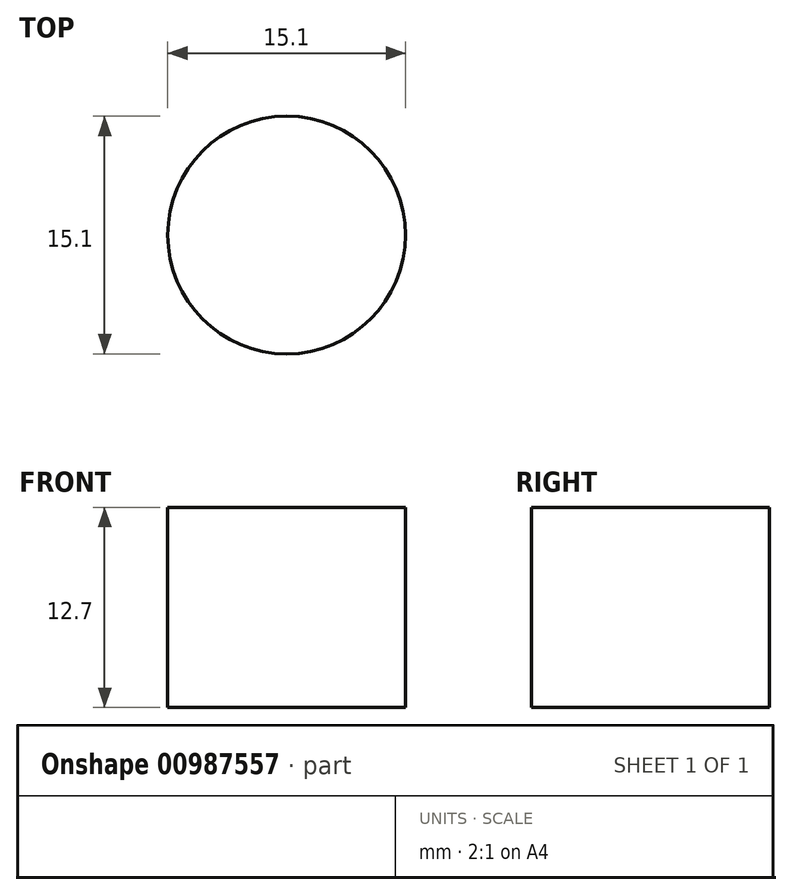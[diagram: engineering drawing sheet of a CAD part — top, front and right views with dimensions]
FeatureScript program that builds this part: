
annotation { "Feature Type Name" : "Feature", "Feature Type Description" : "" }
export const myFeature = defineFeature(function(context is Context, id is Id, definition is map)
    precondition{}
    {
        {
            var Q0;
            Q0=qCreatedBy(makeId("Top.planeOp"),FACE);
            var sketch = newSketch(context, id + "F0", { "sketchPlane" : qUnion([Q0])});
            skCircle(sketch, "E0", {"center": v(0, 0) * mm, "radius": 7.55 * mm});
            skSolve(sketch);
        }
        {
            var Q0;
            Q0 = qSketchRegion(id + "F0", true);
            extrude(context, id + "F1", {"entities" : qUnion([Q0]), "depth" : 12.7 * mm, "offsetDistance" : 25.4 * mm});
        }
    });
